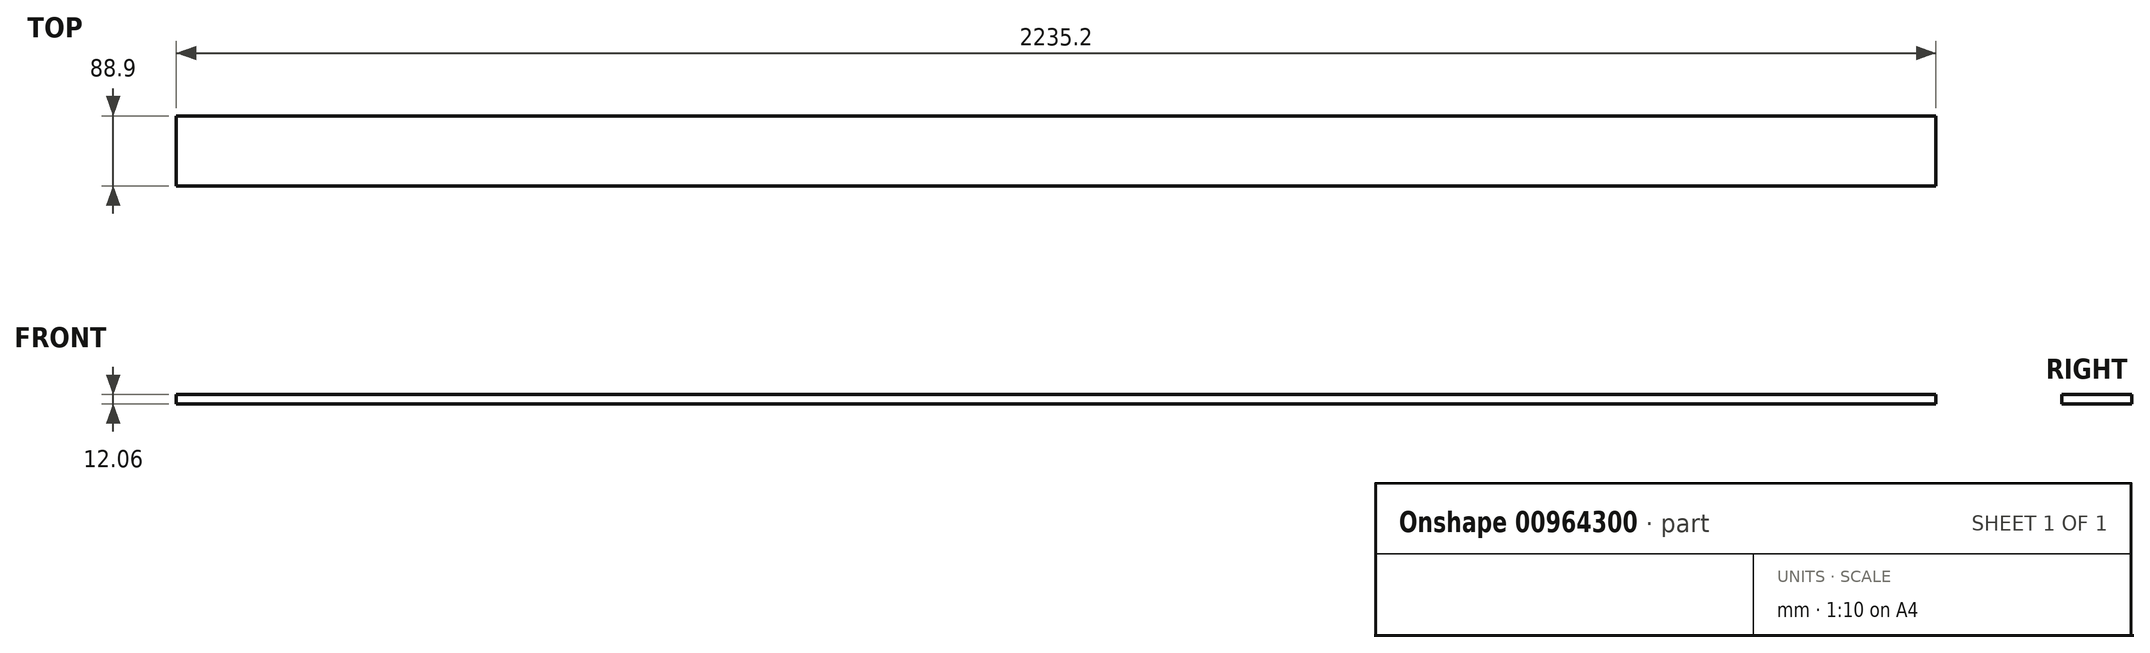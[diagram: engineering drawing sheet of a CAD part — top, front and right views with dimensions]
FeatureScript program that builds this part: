
annotation { "Feature Type Name" : "Feature", "Feature Type Description" : "" }
export const myFeature = defineFeature(function(context is Context, id is Id, definition is map)
    precondition{}
    {
        {
            var Q0;
            Q0=qCreatedBy(makeId("Right.planeOp"),FACE);
            var sketch = newSketch(context, id + "F0", { "sketchPlane" : qUnion([Q0])});
            skLineSegment(sketch, "E0.bottom", {"start": v(-44.45, 6.03) * mm, "end": v(44.45, 6.03) * mm});
            skLineSegment(sketch, "E0.top", {"start": v(-44.45, -6.03) * mm, "end": v(44.45, -6.03) * mm});
            skLineSegment(sketch, "E0.left", {"start": v(-44.45, 6.03) * mm, "end": v(-44.45, -6.03) * mm});
            skLineSegment(sketch, "E0.right", {"start": v(44.45, 6.03) * mm, "end": v(44.45, -6.03) * mm});
            skPoint(sketch, "E0.middle", {"position": v(0, 0) * mm});
            skSolve(sketch);
        }
        {
            var Q0;
            Q0 = qSketchRegion(id + "F0", true);
            extrude(context, id + "F1", {"entities" : qUnion([Q0]), "endBound" : BoundingType.SYMMETRIC, "depth" : 2235.2 * mm, "offsetDistance" : 25.4 * mm});
        }
    });
